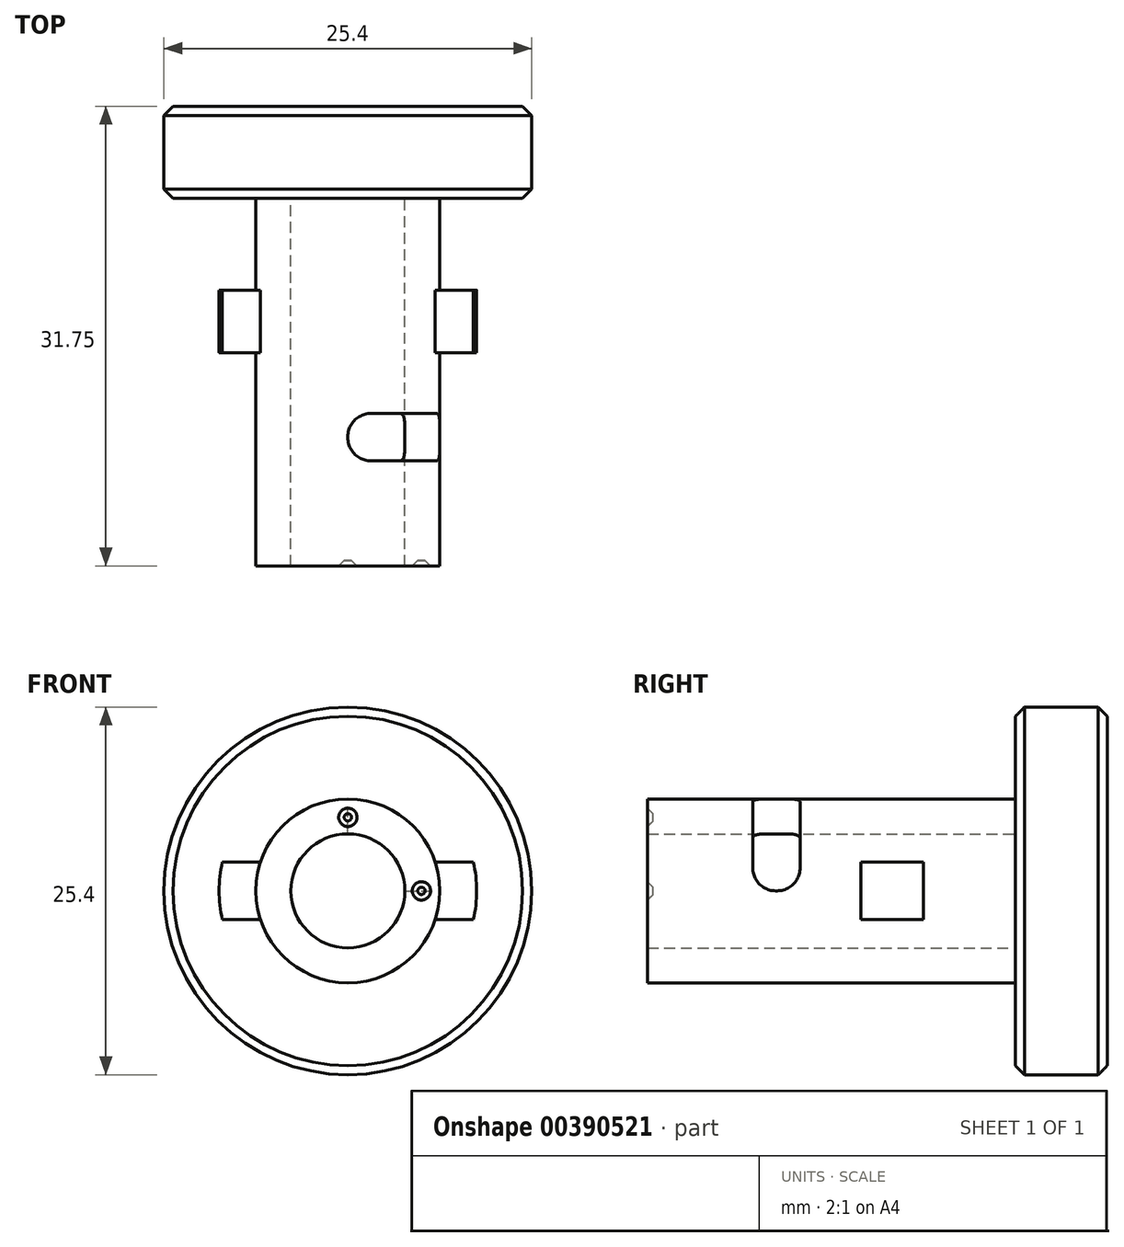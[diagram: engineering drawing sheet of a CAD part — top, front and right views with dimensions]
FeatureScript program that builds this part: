
annotation { "Feature Type Name" : "Feature", "Feature Type Description" : "" }
export const myFeature = defineFeature(function(context is Context, id is Id, definition is map)
    precondition{}
    {
        {
            var Q0;
            Q0=qCreatedBy(makeId("Right.planeOp"),FACE);
            var sketch = newSketch(context, id + "F0", { "sketchPlane" : qUnion([Q0])});
            skLineSegment(sketch, "E0", {"start": v(0, 6.35) * mm, "end": v(25.4, 6.35) * mm});
            skLineSegment(sketch, "E1", {"start": v(25.4, 6.35) * mm, "end": v(25.4, 12.7) * mm});
            skLineSegment(sketch, "E2", {"start": v(25.4, 12.7) * mm, "end": v(31.75, 12.7) * mm});
            skLineSegment(sketch, "E3", {"start": v(31.75, 12.7) * mm, "end": v(31.75, 0) * mm});
            skLineSegment(sketch, "E4", {"start": v(31.75, 0) * mm, "end": v(25.4, 0) * mm});
            skLineSegment(sketch, "E5", {"start": v(25.4, 0) * mm, "end": v(25.4, 3.94) * mm});
            skLineSegment(sketch, "E6", {"start": v(25.4, 3.94) * mm, "end": v(0, 3.94) * mm});
            skLineSegment(sketch, "E7", {"start": v(0, 3.94) * mm, "end": v(0, 6.35) * mm});
            skSolve(sketch);
        }
        {
            var Q0;
            Q0 = qSketchRegion(id + "F0", true);
            var Q1;
            Q1=sQuery(id+"F0.wireOp",EDGE,"E4");
            revolve(context, id + "F1", {"entities" : qUnion([Q0]), "axis" : qUnion([Q1]), "revolveType" : RevolveType.FULL});
        }
        {
            var Q0;
            Q0=makeQuery(id+"F1.opRevolve","SWEPT_EDGE",EDGE,{"disambiguationData":[OSD([sQuery(id+"F0.wireOp",EDGE,"E2"),sQuery(id+"F0.wireOp",EDGE,"E3")])]});
            var Q1;
            Q1=makeQuery(id+"F1.opRevolve","SWEPT_EDGE",EDGE,{"disambiguationData":[OSD([sQuery(id+"F0.wireOp",EDGE,"E1"),sQuery(id+"F0.wireOp",EDGE,"E2")])]});
            chamfer(context, id + "F2", {"entities" : qUnion([Q0, Q1]), "width" : 0.64 * mm, "tangentPropagation" : true});
        }
        {
            var Q0;
            Q0=makeQuery(id+"F1.opRevolve","SWEPT_FACE",FACE,{"disambiguationData":[OSD([sQuery(id+"F0.wireOp",EDGE,"E7")])]});
            var sketch = newSketch(context, id + "F3", { "sketchPlane" : qUnion([Q0])});
            skCircle(sketch, "E8", {"center": v(0, 5.08) * mm, "radius": 0.64 * mm});
            skCircle(sketch, "E9", {"center": v(5.08, 0) * mm, "radius": 0.64 * mm});
            skSolve(sketch);
        }
        {
            var Q0;
            Q0 = qSketchRegion(id + "F3", true);
            extrude(context, id + "F4", {"entities" : qUnion([Q0]), "operationType" : NewBodyOperationType.REMOVE, "oppositeDirection" : true, "depth" : 0.38 * mm});
        }
        {
            var Q0;
            Q0=makeQuery(id+"F4.boolean.opBoolean","COPY",FACE,{"derivedFrom":makeQuery(id+"F4.opExtrude","CAP_FACE",FACE,{"disambiguationData":[OSD([sQuery(id+"F3.wireOp",EDGE,"E8")])],"isStart":false})});
            var Q1;
            Q1=makeQuery(id+"F4.boolean.opBoolean","COPY",FACE,{"derivedFrom":makeQuery(id+"F4.opExtrude","CAP_FACE",FACE,{"disambiguationData":[OSD([sQuery(id+"F3.wireOp",EDGE,"E9")])],"isStart":false})});
            chamfer(context, id + "F5", {"entities" : qUnion([Q0, Q1]), "width" : 0.38 * mm, "tangentPropagation" : true});
        }
        {
            var Q0;
            Q0=qCreatedBy(makeId("Right.planeOp"),FACE);
            var sketch = newSketch(context, id + "F6", { "sketchPlane" : qUnion([Q0])});
            skLineSegment(sketch, "E10.bottom", {"start": v(7.25, 0) * mm, "end": v(10.53, 0) * mm});
            skLineSegment(sketch, "E10.top", {"start": v(7.25, 10.76) * mm, "end": v(10.53, 10.76) * mm});
            skLineSegment(sketch, "E10.left", {"start": v(7.25, 0) * mm, "end": v(7.25, 10.76) * mm});
            skLineSegment(sketch, "E10.right", {"start": v(10.53, 0) * mm, "end": v(10.53, 10.76) * mm});
            skPoint(sketch, "E11", {"position": v(8.9, 0) * mm});
            skSolve(sketch);
        }
        {
            var Q0;
            Q0 = qSketchRegion(id + "F6", true);
            var Q1;
            Q1=makeQuery(id+"F1.opRevolve","SWEPT_EDGE",EDGE,{"disambiguationData":[OSD([sQuery(id+"F0.wireOp",EDGE,"E6"),sQuery(id+"F0.wireOp",EDGE,"E7")])]});
            revolve(context, id + "F7", {"operationType" : NewBodyOperationType.REMOVE, "entities" : qUnion([Q0]), "axis" : qUnion([Q1]), "revolveType" : RevolveType.ONE_DIRECTION, "angle" : 90 * degree});
        }
        {
            var Q0;
            Q0=makeQuery(id+"F1.opRevolve","SWEPT_FACE",FACE,{"disambiguationData":[OSD([sQuery(id+"F0.wireOp",EDGE,"E1")])]});
            cPlane(context, id + "F8", {"entities" : qUnion([Q0]), "cplaneType" : CPlaneType.OFFSET, "offset" : 6.35 * mm, "width" : 152.4 * mm, "height" : 152.4 * mm});
        }
        {
            var Q0;
            Q0=qCreatedBy(id+"F8.planeOp",FACE);
            var sketch = newSketch(context, id + "F9", { "sketchPlane" : qUnion([Q0])});
            skArc(sketch, "E12", {"start": v(-8.67, 1.98) * mm, "mid": v(-8.89, 0) * mm, "end": v(-8.67, -1.98) * mm});
            skLineSegment(sketch, "E13", {"start": v(8.67, -1.98) * mm, "end": v(5.45, -1.98) * mm});
            skLineSegment(sketch, "E14", {"start": v(5.45, -1.98) * mm, "end": v(5.45, 1.98) * mm});
            skLineSegment(sketch, "E15", {"start": v(5.45, 1.98) * mm, "end": v(8.67, 1.98) * mm});
            skLineSegment(sketch, "E16", {"start": v(0, 14.74) * mm, "end": v(0, -15.84) * mm});
            skLineSegment(sketch, "E17.MirrorCS", {"start": v(-5.45, 1.98) * mm, "end": v(-8.67, 1.98) * mm});
            skLineSegment(sketch, "E18.MirrorCS", {"start": v(-5.45, -1.98) * mm, "end": v(-5.45, 1.98) * mm});
            skLineSegment(sketch, "E19.MirrorCS", {"start": v(-8.67, -1.98) * mm, "end": v(-5.45, -1.98) * mm});
            skArc(sketch, "E20.trimOffspring", {"start": v(8.67, -1.98) * mm, "mid": v(8.89, 0) * mm, "end": v(8.67, 1.98) * mm});
            skSolve(sketch);
        }
        {
            var Q0;
            Q0=makeQuery(id+"F9.imprint","IMPRINT",FACE,{"disambiguationData":[TD([[makeQuery(id+"F9.imprint","IMPRINT",EDGE,{"derivedFrom":sQuery(id+"F9.wireOp",EDGE,"E13")}),-1.0]])]});
            var Q1;
            Q1=makeQuery(id+"F9.imprint","IMPRINT",FACE,{"disambiguationData":[TD([[makeQuery(id+"F9.imprint","IMPRINT",EDGE,{"derivedFrom":sQuery(id+"F9.wireOp",EDGE,"E12")}),1.0]])]});
            extrude(context, id + "F10", {"entities" : qUnion([Q0, Q1]), "operationType" : NewBodyOperationType.ADD, "depth" : 4.32 * mm});
        }
        {
            var Q0;
            Q0=makeQuery(id+"F7.boolean.opBoolean","COPY",EDGE,{"derivedFrom":makeQuery(id+"F7.opRevolve","CAP_EDGE",EDGE,{"disambiguationData":[OSD([sQuery(id+"F6.wireOp",EDGE,"E10.right")])],"isStart":true})});
            var Q1;
            Q1=makeQuery(id+"F7.boolean.opBoolean","COPY",EDGE,{"derivedFrom":makeQuery(id+"F7.opRevolve","CAP_EDGE",EDGE,{"disambiguationData":[OSD([sQuery(id+"F6.wireOp",EDGE,"E10.left")])],"isStart":true})});
            var Q2;
            Q2=makeQuery(id+"F7.boolean.opBoolean","COPY",EDGE,{"derivedFrom":makeQuery(id+"F7.opRevolve","CAP_EDGE",EDGE,{"disambiguationData":[OSD([sQuery(id+"F6.wireOp",EDGE,"E10.right")])],"isStart":false})});
            var Q3;
            Q3=makeQuery(id+"F7.boolean.opBoolean","COPY",EDGE,{"derivedFrom":makeQuery(id+"F7.opRevolve","CAP_EDGE",EDGE,{"disambiguationData":[OSD([sQuery(id+"F6.wireOp",EDGE,"E10.left")])],"isStart":false})});
            fillet(context, id + "F11", {"entities" : qUnion([Q0, Q1, Q2, Q3]), "radius" : 1.6 * mm, "tangentPropagation" : true, "allowEdgeOverflow" : false});
        }
    });
